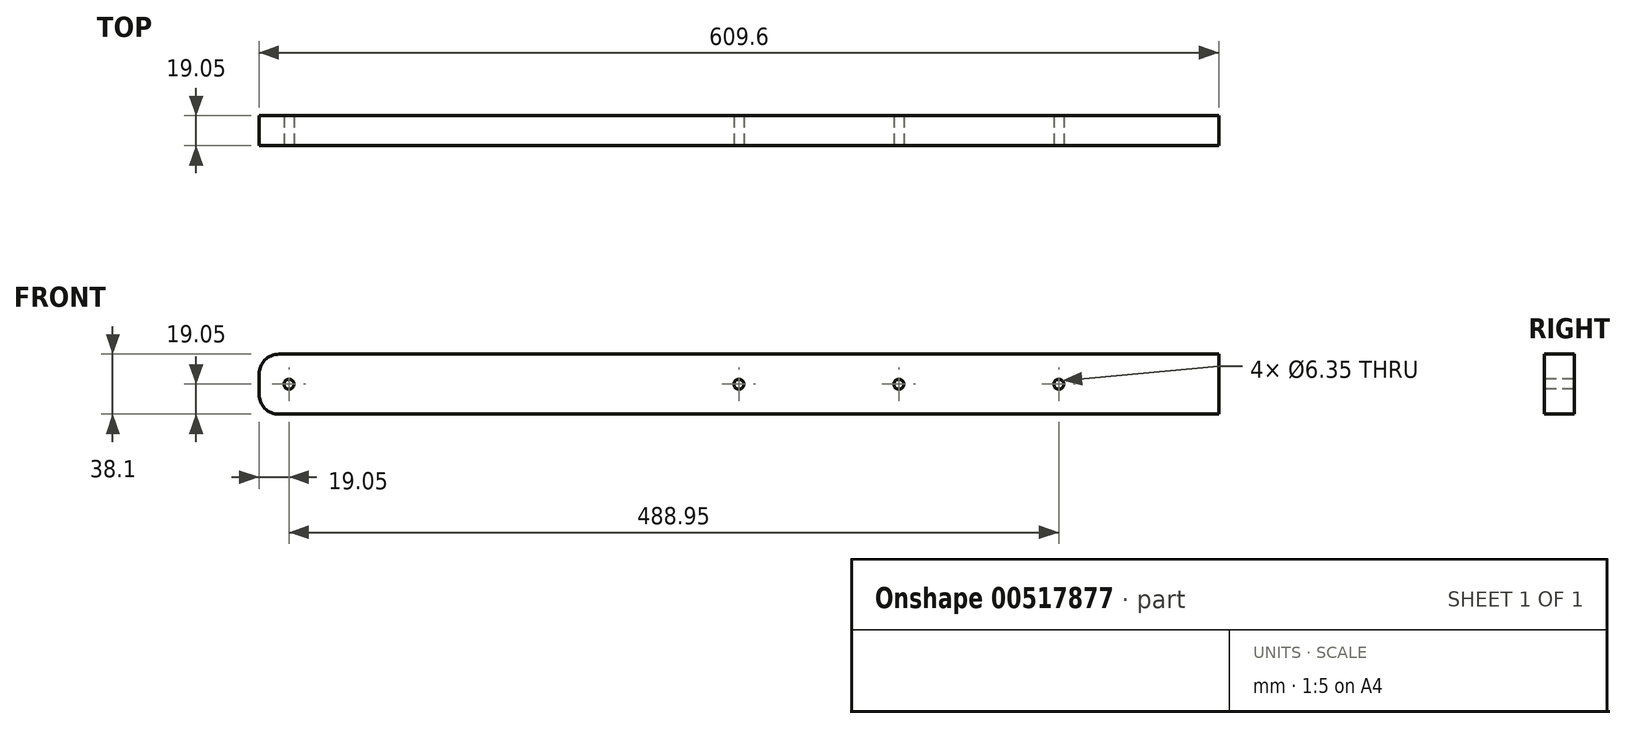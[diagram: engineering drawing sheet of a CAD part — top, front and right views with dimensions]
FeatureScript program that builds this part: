
annotation { "Feature Type Name" : "Feature", "Feature Type Description" : "" }
export const myFeature = defineFeature(function(context is Context, id is Id, definition is map)
    precondition{}
    {
        {
            var Q0;
            Q0=qCreatedBy(makeId("Right.planeOp"),FACE);
            var sketch = newSketch(context, id + "F0", { "sketchPlane" : qUnion([Q0])});
            skLineSegment(sketch, "E0.bottom", {"start": v(0, 0) * mm, "end": v(19.05, 0) * mm});
            skLineSegment(sketch, "E0.top", {"start": v(0, 38.1) * mm, "end": v(19.05, 38.1) * mm});
            skLineSegment(sketch, "E0.left", {"start": v(0, 0) * mm, "end": v(0, 38.1) * mm});
            skLineSegment(sketch, "E0.right", {"start": v(19.05, 0) * mm, "end": v(19.05, 38.1) * mm});
            skSolve(sketch);
        }
        {
            var Q0;
            Q0=makeQuery(id+"F0.imprint","IMPRINT",FACE,{"disambiguationData":[TD([[makeQuery(id+"F0.imprint","IMPRINT",EDGE,{"derivedFrom":sQuery(id+"F0.wireOp",EDGE,"E0.bottom")}),1.0]])]});
            extrude(context, id + "F1", {"entities" : qUnion([Q0]), "oppositeDirection" : true, "depth" : 609.6 * mm, "offsetDistance" : 25.4 * mm});
        }
        {
            var Q0;
            Q0=makeQuery(id+"F1.opExtrude","SWEPT_FACE",FACE,{"disambiguationData":[OSD([sQuery(id+"F0.wireOp",EDGE,"E0.left")])]});
            var sketch = newSketch(context, id + "F2", { "sketchPlane" : qUnion([Q0])});
            skCircle(sketch, "E1", {"center": v(-609.6, 19.05) * mm, "radius": 3.18 * mm, "construction": true});
            skCircle(sketch, "E2.1.0.0", {"center": v(-590.55, 19.05) * mm, "radius": 3.18 * mm});
            skLineSegment(sketch, "E2.direction1", {"start": v(-609.6, 19.05) * mm, "end": v(-590.55, 19.05) * mm, "construction": true});
            skCircle(sketch, "E3", {"center": v(0, 19.05) * mm, "radius": 3.18 * mm, "construction": true});
            skCircle(sketch, "E4.1.0.0", {"center": v(-101.6, 19.05) * mm, "radius": 3.18 * mm});
            skCircle(sketch, "E4.2.0.0", {"center": v(-203.2, 19.05) * mm, "radius": 3.18 * mm});
            skCircle(sketch, "E4.3.0.0", {"center": v(-304.8, 19.05) * mm, "radius": 3.18 * mm});
            skLineSegment(sketch, "E4.direction1", {"start": v(0, 19.05) * mm, "end": v(-101.6, 19.05) * mm, "construction": true});
            skSolve(sketch);
        }
        {
            var Q0;
            Q0=makeQuery(id+"F2.imprint","IMPRINT",FACE,{"disambiguationData":[TD([[makeQuery(id+"F2.imprint","IMPRINT",EDGE,{"derivedFrom":sQuery(id+"F2.wireOp",EDGE,"E4.1.0.0")}),1.0]])]});
            var Q1;
            Q1=makeQuery(id+"F2.imprint","IMPRINT",FACE,{"disambiguationData":[TD([[makeQuery(id+"F2.imprint","IMPRINT",EDGE,{"derivedFrom":sQuery(id+"F2.wireOp",EDGE,"E4.2.0.0")}),1.0]])]});
            var Q2;
            Q2=makeQuery(id+"F2.imprint","IMPRINT",FACE,{"disambiguationData":[TD([[makeQuery(id+"F2.imprint","IMPRINT",EDGE,{"derivedFrom":sQuery(id+"F2.wireOp",EDGE,"E4.3.0.0")}),1.0]])]});
            var Q3;
            Q3=makeQuery(id+"F2.imprint","IMPRINT",FACE,{"disambiguationData":[TD([[makeQuery(id+"F2.imprint","IMPRINT",EDGE,{"derivedFrom":sQuery(id+"F2.wireOp",EDGE,"E2.1.0.0")}),1.0]])]});
            extrude(context, id + "F3", {"entities" : qUnion([Q0, Q1, Q2, Q3]), "operationType" : NewBodyOperationType.REMOVE, "endBound" : BoundingType.THROUGH_ALL, "oppositeDirection" : true, "depth" : 25.4 * mm, "offsetDistance" : 25.4 * mm});
        }
        {
            var Q0;
            Q0=makeQuery(id+"F1.opExtrude","CAP_EDGE",EDGE,{"disambiguationData":[OSD([sQuery(id+"F0.wireOp",EDGE,"E0.top")])],"isStart":false});
            var Q1;
            Q1=makeQuery(id+"F1.opExtrude","CAP_EDGE",EDGE,{"disambiguationData":[OSD([sQuery(id+"F0.wireOp",EDGE,"E0.bottom")])],"isStart":false});
            fillet(context, id + "F4", {"entities" : qUnion([Q0, Q1]), "radius" : 12.7 * mm, "tangentPropagation" : true, "allowEdgeOverflow" : false});
        }
    });
